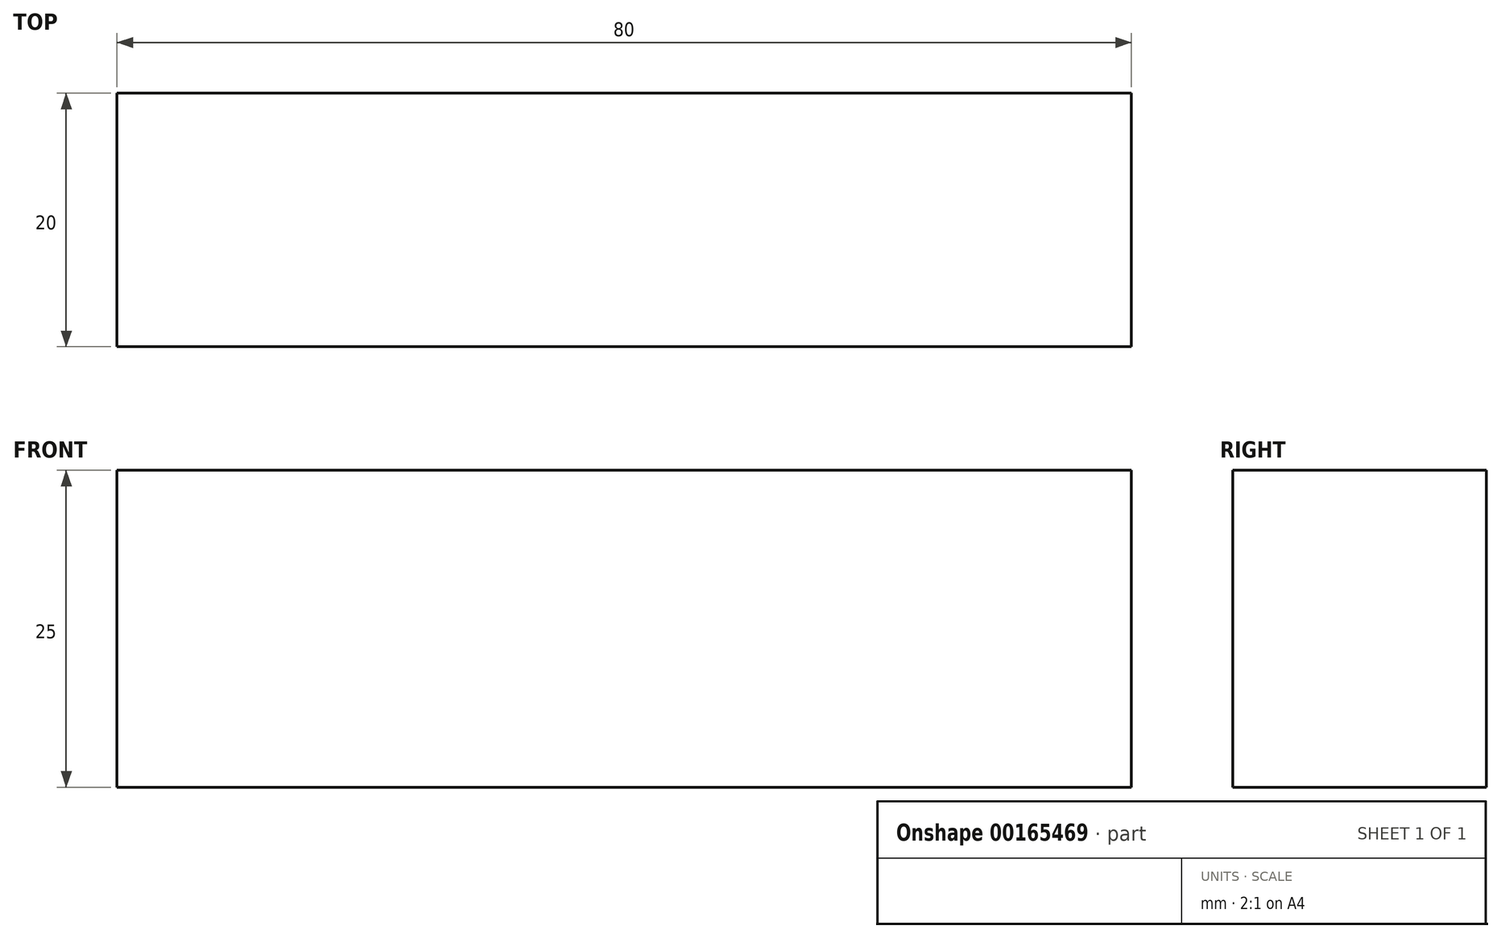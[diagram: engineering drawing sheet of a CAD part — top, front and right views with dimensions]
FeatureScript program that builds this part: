
annotation { "Feature Type Name" : "Feature", "Feature Type Description" : "" }
export const myFeature = defineFeature(function(context is Context, id is Id, definition is map)
    precondition{}
    {
        {
            var Q0;
            Q0=qCreatedBy(makeId("Top.planeOp"),FACE);
            var sketch = newSketch(context, id + "F0", { "sketchPlane" : qUnion([Q0])});
            skLineSegment(sketch, "E0.bottom", {"start": v(0, 0) * mm, "end": v(80, 0) * mm});
            skLineSegment(sketch, "E0.top", {"start": v(0, 20) * mm, "end": v(80, 20) * mm});
            skLineSegment(sketch, "E0.left", {"start": v(0, 0) * mm, "end": v(0, 20) * mm});
            skLineSegment(sketch, "E0.right", {"start": v(80, 0) * mm, "end": v(80, 20) * mm});
            skSolve(sketch);
        }
        {
            var Q0;
            Q0=makeQuery(id+"F0.imprint","IMPRINT",FACE,{"disambiguationData":[TD([[makeQuery(id+"F0.imprint","IMPRINT",EDGE,{"derivedFrom":sQuery(id+"F0.wireOp",EDGE,"E0.bottom")}),1.0]])]});
            extrude(context, id + "F1", {"entities" : qUnion([Q0]), "depth" : 25 * mm, "offsetDistance" : 25 * mm});
        }
    });
